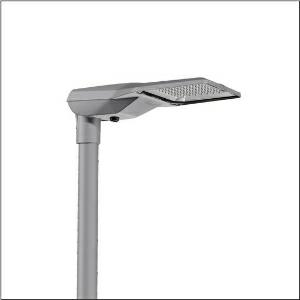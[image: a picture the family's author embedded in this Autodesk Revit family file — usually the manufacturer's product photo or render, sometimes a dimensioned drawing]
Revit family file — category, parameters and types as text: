
# Revit family: streetlight_sl_21_midi___st1_0a_5xe3d33r08lb_2d19
name_source: partatom
category: Lighting Fixtures
units: mm (PartAtom-declared; Revit-internal decimal feet)

## family parameters
Cut with Voids When Loaded = No
Host = Face
Light Source = No
Part Type = Normal
Room Calculation Point = No
Round Connector Dimension = Use Diameter
Shared = No

## types (1)
- --- (1 x LED, 14340 lm, 99.6 W, 3000K)
    Apparent Load = 100 VA
    CIE Flux Codes = 37 72 97 100 100
    Color Rendering = 70
    Color Temperature = 3000K
    Default Elevation = 1800 mm
    Description = Streetlight SL 21 midi, mast luminaire, primary light control with lens, of PMMA, primary optical cover: cover, of toughened safety glass, transparent, light distribution: ST1.0a, light emission: direct distribution, primary light characteristic: asymmetric, installation type: side-entry, post-top, LED, High Power LED, rated luminous flux: 14.340lm, luminous efficacy: 144lm/W, light colour: 730, colour temperature: 3000K, control gear: D4i, control: flexible luminous flux parameterisation, time-dependent luminous flux control, constant luminous flux control, overheat protection, pre-setting: logarithmic dimming characteristic, mains connection: 230..240V, AC, 50/60Hz, start of lifetime: 100W, end of service life: 102W, reduction: 46W, luminaire housing, of diecast aluminium, powder-coated, SITECO metallic grey (DB 702S), corrosivity category C5 high according to DIN EN ISO 12944, please order mast flange separately, inclination adjustable: 0°, 5°, 10°, 15°, sealing non-destructively replaceable, multi-level sealing system, length: 644mm, width: 335mm, height: 110mm, mast flange for spigot size: 42mm (side-entry): 5XC10008XM4, 60/48mm (side-entry/post-top): 5XC10108XM2, 76/60mm (side-entry/post-top): 5XC10108XM1, mounting height: 4..8m, Smart Interface below, protection rating (complete): IP66, insulation class (complete): insulation class II (safety insulation), certification: CE, ENEC, ENEC+, VDE, impact resistance: IK10, permissible operating ambient temperature for outdoor applications: -40..+50°C, standard-compliant lighting for roads and squares, packaging unit: 1 piece

Light Distribution: ST1.0a
    Height = 111 mm
    Lamp = 1 x LED
    Lamp Light Flux = 14340 lm
    Lamp Power = 99.6 W
    Lamp count = 1
    Length = 644 mm
    Luminous efficacy = 144 lm/W
    Manufacturer = Siteco
    ModVariant = No
    Model = 5XE3D33R08LB
    Number of Poles = 1
    OnlyDefault = Yes
    Power Factor = 1
    Product Name = Streetlight SL 21 midi | ST1.0a
    Product group = mast luminaire | pylon top
    ProductGroupID = 6100
    Protection Class = Protection class II
    Protection Degree = IP 66
    RLX_Detail_Level = 1
    RLX_Emergency_Light_Flux = 0 lm
    RLX_Emergency_Type = 0
    RLX_Emergency_Type_DB = No
    RlxData = <blob elided: 26893 chars, md5=ebb53b34>
    Socket = socket
    Standby Power = 0 W
    System Light Flux = 14340 lm
    System Power = 100 W
    Type Comments = factory setting: luminous flux: 100 % | dim-lin: 254 | 1020 mA
    Type Image = l_1004300.jpg
    URL = http://relux.com
    VarID = @adj_031805
    Voltage = 0 V
    Weight = 0.00 kg
    Width = 336 mm

## geometry (parser evidence)
native form markers: Blend x4, Sweep x10
no freeform markers — native parametric forms only
